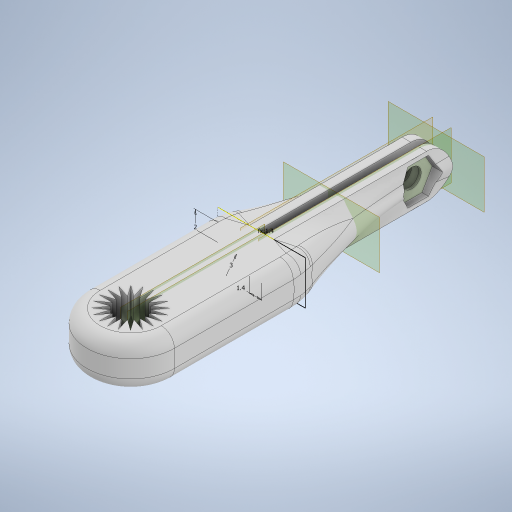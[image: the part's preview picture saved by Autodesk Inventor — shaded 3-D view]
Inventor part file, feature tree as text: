
AUTODESK INVENTOR PART (.ipt)
format: ipt  version: 2023.1 (Build 271208000, 208)  size: 770,048 bytes
history: native  units: mm
features: extrude x8, plane x7, sketch x7, other x4, projected_geometry x4, fillet x3, loft x2
ambient origin geometry x8: Origin, YZ Plane, XZ Plane, XY Plane, X Axis, Y Axis, Z Axis, Center Point
bodies: Solid1 (feature_tree)
feature tree (35):
  extrude  "Horn Base"  Depth=20.0mm
  extrude  "Servo Spline Cut"  Depth=2.0mm TaperAngle=0.0deg
  plane  "Work Plane (Clip Axis)"
  sketch  "Sketch5"  dims[d0=10.0mm d1=20.0mm]
  plane  "Work Plane2"
  sketch  "Sketch6"  dims[d2=3.0mm d3=2.0mm d4=0.0mm]
  plane  "Work Plane3"
  sketch  "Sketch7"  dims[d5=3.3mm d6=1.5mm]
  plane  "Work Plane4"
  sketch  "Sketch8"  dims[d7=3.141593mm d9=200.0mm d11=360.0deg]
  extrude  "Extrusion3"  Depth=1.5mm
  plane  "Work Plane5"
  extrude  "Extrusion4"  Depth=200.0mm TaperAngle=360.0deg
  loft  "Loft4"
  loft  "Loft5"
  fillet  "Fillet4"  Radius=3.0mm
  fillet  "Fillet5"  [1 undecoded]
  plane  "Work Plane6"
  sketch  "Sketch10"  dims[d23=1.4mm d24=2.0mm d25=3.0mm d26=-4.6mm]
  extrude  "Extrusion5"  Depth=20.0mm
  extrude  "Extrusion6"  Depth=8.0mm
  plane  "Work Plane7"
  sketch  "Sketch11"  dims[d27=20.0mm d28=20.0mm d31=8.0mm d32=1.4mm d33=2.0mm d34=1.5mm d35=2.0mm d36=1.4mm d37=0.5mm d38=1.0mm d39=4.0mm d46=1.0mm d47=0.0mm d62=1.4mm d63=-0.8mm d64=1.0mm d65=0.0mm d66=0.0mm d67=90.0deg d68=0.0mm d69=90.0deg d70=0.0mm d71=90.0deg d72=0.0mm d73=90.0deg d74=0.0mm d75=90.0deg d76=0.0mm d77=90.0deg d78=1.5mm d79=2.5mm d80=-1.0mm d81=2.15mm d82=1.0mm d83=45.0deg d84=1.0mm d85=0.0mm d86=-0.3mm d87=2.35mm d92=2.0mm d93=0.0mm d94=3.5mm d95=2.0mm d96=0.0mm d97=8.0mm d60=0.0mm d61=0.0mm d88=0.872665mm d89=0.5mm d90=0.872665mm]
  extrude  "Extrusion8"  Depth=1.4mm
  extrude  "Extrusion9"  Depth=2.0mm
  fillet  "Fillet6"  Radius=1.5mm
  other  "Horn Base Profile"
  other  "Spline Profile"
  sketch  "Sketch9"  dims[d13=3.0mm d14=0.0mm d15=-2.5mm]
  other  "Edges3"
  other  "Edges4"
  projected_geometry  "Project Cut Edges3"
  projected_geometry  "Project Cut Edges4"
  projected_geometry  "Project Cut Edges5"
  projected_geometry  "Project Cut Edges6"
note: 1 required parameter value undecoded (feature->parameter linkage not recoverable at this tier; creation-order binding heuristic only, values carry confidence <= 0.55)
